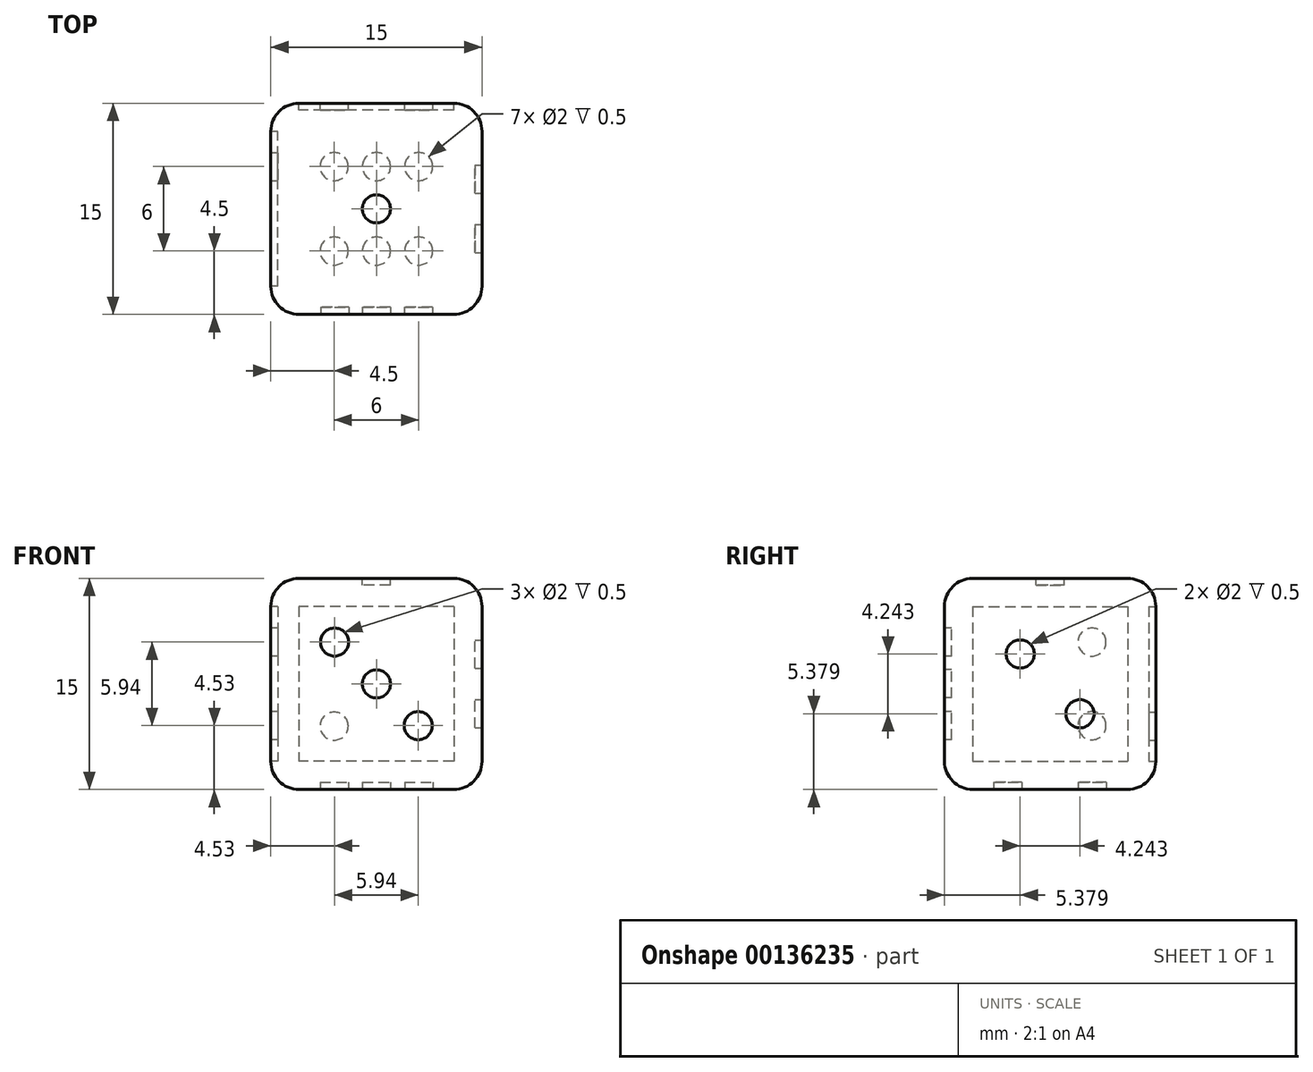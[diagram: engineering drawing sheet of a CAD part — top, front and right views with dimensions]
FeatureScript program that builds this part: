
annotation { "Feature Type Name" : "Feature", "Feature Type Description" : "" }
export const myFeature = defineFeature(function(context is Context, id is Id, definition is map)
    precondition{}
    {
        {
            var Q0;
            Q0=qCreatedBy(makeId("Top.planeOp"),FACE);
            var sketch = newSketch(context, id + "F0", { "sketchPlane" : qUnion([Q0])});
            skLineSegment(sketch, "E0.bottom", {"start": v(0, 0) * mm, "end": v(-15, 0) * mm});
            skLineSegment(sketch, "E0.top", {"start": v(0, 15) * mm, "end": v(-15, 15) * mm});
            skLineSegment(sketch, "E0.left", {"start": v(0, 0) * mm, "end": v(0, 15) * mm});
            skLineSegment(sketch, "E0.right", {"start": v(-15, 0) * mm, "end": v(-15, 15) * mm});
            skSolve(sketch);
        }
        {
            var Q0;
            Q0=makeQuery(id+"F0.imprint","IMPRINT",FACE,{"disambiguationData":[TD([[makeQuery(id+"F0.imprint","IMPRINT",EDGE,{"derivedFrom":sQuery(id+"F0.wireOp",EDGE,"E0.bottom")}),-1.0]])]});
            extrude(context, id + "F1", {"entities" : qUnion([Q0]), "depth" : 15 * mm});
        }
        {
            var Q0;
            Q0=makeQuery(id+"F1.opExtrude","SWEPT_EDGE",EDGE,{"disambiguationData":[OSD([sQuery(id+"F0.wireOp",EDGE,"E0.top"),sQuery(id+"F0.wireOp",EDGE,"E0.right")])]});
            var Q1;
            Q1=makeQuery(id+"F1.opExtrude","SWEPT_EDGE",EDGE,{"disambiguationData":[OSD([sQuery(id+"F0.wireOp",EDGE,"E0.top"),sQuery(id+"F0.wireOp",EDGE,"E0.left")])]});
            var Q2;
            Q2=makeQuery(id+"F1.opExtrude","SWEPT_EDGE",EDGE,{"disambiguationData":[OSD([sQuery(id+"F0.wireOp",EDGE,"E0.bottom"),sQuery(id+"F0.wireOp",EDGE,"E0.left")])]});
            var Q3;
            Q3=makeQuery(id+"F1.opExtrude","CAP_EDGE",EDGE,{"disambiguationData":[OSD([sQuery(id+"F0.wireOp",EDGE,"E0.bottom")])],"isStart":false});
            var Q4;
            Q4=makeQuery(id+"F1.opExtrude","CAP_EDGE",EDGE,{"disambiguationData":[OSD([sQuery(id+"F0.wireOp",EDGE,"E0.top")])],"isStart":true});
            var Q5;
            Q5=makeQuery(id+"F1.opExtrude","CAP_EDGE",EDGE,{"disambiguationData":[OSD([sQuery(id+"F0.wireOp",EDGE,"E0.top")])],"isStart":false});
            var Q6;
            Q6=makeQuery(id+"F1.opExtrude","SWEPT_EDGE",EDGE,{"disambiguationData":[OSD([sQuery(id+"F0.wireOp",EDGE,"E0.bottom"),sQuery(id+"F0.wireOp",EDGE,"E0.right")])]});
            var Q7;
            Q7=makeQuery(id+"F1.opExtrude","CAP_EDGE",EDGE,{"disambiguationData":[OSD([sQuery(id+"F0.wireOp",EDGE,"E0.bottom")])],"isStart":true});
            var Q8;
            Q8=makeQuery(id+"F1.opExtrude","CAP_EDGE",EDGE,{"disambiguationData":[OSD([sQuery(id+"F0.wireOp",EDGE,"E0.left")])],"isStart":true});
            var Q9;
            Q9=makeQuery(id+"F1.opExtrude","CAP_EDGE",EDGE,{"disambiguationData":[OSD([sQuery(id+"F0.wireOp",EDGE,"E0.left")])],"isStart":false});
            var Q10;
            Q10=makeQuery(id+"F1.opExtrude","CAP_EDGE",EDGE,{"disambiguationData":[OSD([sQuery(id+"F0.wireOp",EDGE,"E0.right")])],"isStart":true});
            var Q11;
            Q11=makeQuery(id+"F1.opExtrude","CAP_EDGE",EDGE,{"disambiguationData":[OSD([sQuery(id+"F0.wireOp",EDGE,"E0.right")])],"isStart":false});
            fillet(context, id + "F2", {"entities" : qUnion([Q0, Q1, Q2, Q3, Q4, Q5, Q6, Q7, Q8, Q9, Q10, Q11]), "radius" : 2 * mm, "tangentPropagation" : true, "allowEdgeOverflow" : false});
        }
        {
            var Q0;
            Q0=makeQuery(id+"F1.opExtrude","CAP_FACE",FACE,{"disambiguationData":[OSD([sQuery(id+"F0.wireOp",EDGE,"E0.bottom"),sQuery(id+"F0.wireOp",EDGE,"E0.top"),sQuery(id+"F0.wireOp",EDGE,"E0.left"),sQuery(id+"F0.wireOp",EDGE,"E0.right")])],"isStart":false});
            var sketch = newSketch(context, id + "F3", { "sketchPlane" : qUnion([Q0])});
            skCircle(sketch, "E1", {"center": v(-7.5, 7.5) * mm, "radius": 1 * mm});
            skPoint(sketch, "E1.centerSnap0", {"position": v(-13, 7.5) * mm});
            skSolve(sketch);
        }
        {
            var Q0;
            Q0=makeQuery(id+"F3.imprint","IMPRINT",FACE,{"disambiguationData":[TD([[makeQuery(id+"F3.imprint","IMPRINT",EDGE,{"derivedFrom":sQuery(id+"F3.wireOp",EDGE,"E1")}),1.0]])]});
            extrude(context, id + "F4", {"entities" : qUnion([Q0]), "operationType" : NewBodyOperationType.REMOVE, "oppositeDirection" : true, "depth" : 0.5 * mm});
        }
        {
            var Q0;
            Q0=makeQuery(id+"F1.opExtrude","CAP_FACE",FACE,{"disambiguationData":[OSD([sQuery(id+"F0.wireOp",EDGE,"E0.bottom"),sQuery(id+"F0.wireOp",EDGE,"E0.top"),sQuery(id+"F0.wireOp",EDGE,"E0.left"),sQuery(id+"F0.wireOp",EDGE,"E0.right")])],"isStart":true});
            var sketch = newSketch(context, id + "F5", { "sketchPlane" : qUnion([Q0])});
            skLineSegment(sketch, "E2", {"start": v(-13, -4.5) * mm, "end": v(-2, -4.5) * mm, "construction": true});
            skLineSegment(sketch, "E3", {"start": v(-13, -10.5) * mm, "end": v(-2, -10.5) * mm, "construction": true});
            skCircle(sketch, "E4", {"center": v(-10.5, -4.5) * mm, "radius": 1 * mm});
            skCircle(sketch, "E5", {"center": v(-7.5, -4.5) * mm, "radius": 1 * mm});
            skCircle(sketch, "E6", {"center": v(-4.5, -4.5) * mm, "radius": 1 * mm});
            skCircle(sketch, "E7", {"center": v(-10.5, -10.5) * mm, "radius": 1 * mm});
            skCircle(sketch, "E8", {"center": v(-7.5, -10.5) * mm, "radius": 1 * mm});
            skCircle(sketch, "E9", {"center": v(-4.5, -10.5) * mm, "radius": 1 * mm});
            skSolve(sketch);
        }
        {
            var Q0;
            Q0=makeQuery(id+"F5.imprint","IMPRINT",FACE,{"disambiguationData":[TD([[makeQuery(id+"F5.imprint","IMPRINT",EDGE,{"derivedFrom":sQuery(id+"F5.wireOp",EDGE,"E9")}),1.0]])]});
            var Q1;
            Q1=makeQuery(id+"F5.imprint","IMPRINT",FACE,{"disambiguationData":[TD([[makeQuery(id+"F5.imprint","IMPRINT",EDGE,{"derivedFrom":sQuery(id+"F5.wireOp",EDGE,"E8")}),1.0]])]});
            var Q2;
            Q2=makeQuery(id+"F5.imprint","IMPRINT",FACE,{"disambiguationData":[TD([[makeQuery(id+"F5.imprint","IMPRINT",EDGE,{"derivedFrom":sQuery(id+"F5.wireOp",EDGE,"E7")}),1.0]])]});
            var Q3;
            Q3=makeQuery(id+"F5.imprint","IMPRINT",FACE,{"disambiguationData":[TD([[makeQuery(id+"F5.imprint","IMPRINT",EDGE,{"derivedFrom":sQuery(id+"F5.wireOp",EDGE,"E4")}),1.0]])]});
            var Q4;
            Q4=makeQuery(id+"F5.imprint","IMPRINT",FACE,{"disambiguationData":[TD([[makeQuery(id+"F5.imprint","IMPRINT",EDGE,{"derivedFrom":sQuery(id+"F5.wireOp",EDGE,"E5")}),1.0]])]});
            var Q5;
            Q5=makeQuery(id+"F5.imprint","IMPRINT",FACE,{"disambiguationData":[TD([[makeQuery(id+"F5.imprint","IMPRINT",EDGE,{"derivedFrom":sQuery(id+"F5.wireOp",EDGE,"E6")}),1.0]])]});
            extrude(context, id + "F6", {"entities" : qUnion([Q0, Q1, Q2, Q3, Q4, Q5]), "operationType" : NewBodyOperationType.REMOVE, "oppositeDirection" : true, "depth" : 0.5 * mm});
        }
        {
            var Q0;
            Q0=makeQuery(id+"F1.opExtrude","SWEPT_FACE",FACE,{"disambiguationData":[OSD([sQuery(id+"F0.wireOp",EDGE,"E0.top")])]});
            var sketch = newSketch(context, id + "F7", { "sketchPlane" : qUnion([Q0])});
            skLineSegment(sketch, "E10", {"start": v(2, 10.5) * mm, "end": v(13, 10.5) * mm, "construction": true});
            skCircle(sketch, "E11", {"center": v(4.5, 10.5) * mm, "radius": 1 * mm});
            skCircle(sketch, "E12", {"center": v(10.5, 10.5) * mm, "radius": 1 * mm});
            skLineSegment(sketch, "E13", {"start": v(2, 7.5) * mm, "end": v(13, 7.5) * mm, "construction": true});
            skCircle(sketch, "E14.MirrorC", {"center": v(10.5, 4.5) * mm, "radius": 1 * mm});
            skCircle(sketch, "E15.MirrorC", {"center": v(4.5, 4.5) * mm, "radius": 1 * mm});
            skLineSegment(sketch, "E16.MirrorCS", {"start": v(2, 4.5) * mm, "end": v(13, 4.5) * mm, "construction": true});
            skSolve(sketch);
        }
        {
            var Q0;
            Q0=makeQuery(id+"F7.imprint","IMPRINT",FACE,{"disambiguationData":[TD([[makeQuery(id+"F7.imprint","IMPRINT",EDGE,{"derivedFrom":sQuery(id+"F7.wireOp",EDGE,"E12")}),1.0]])]});
            var Q1;
            Q1=makeQuery(id+"F7.imprint","IMPRINT",FACE,{"disambiguationData":[TD([[makeQuery(id+"F7.imprint","IMPRINT",EDGE,{"derivedFrom":sQuery(id+"F7.wireOp",EDGE,"E11")}),1.0]])]});
            var Q2;
            Q2=makeQuery(id+"F7.imprint","IMPRINT",FACE,{"disambiguationData":[TD([[makeQuery(id+"F7.imprint","IMPRINT",EDGE,{"derivedFrom":sQuery(id+"F7.wireOp",EDGE,"E15.MirrorC")}),-1.0]])]});
            var Q3;
            Q3=makeQuery(id+"F7.imprint","IMPRINT",FACE,{"disambiguationData":[TD([[makeQuery(id+"F7.imprint","IMPRINT",EDGE,{"derivedFrom":sQuery(id+"F7.wireOp",EDGE,"E14.MirrorC")}),-1.0]])]});
            extrude(context, id + "F8", {"entities" : qUnion([Q0, Q1, Q2, Q3]), "operationType" : NewBodyOperationType.REMOVE, "oppositeDirection" : true, "depth" : 0.5 * mm});
        }
        {
            var Q0;
            Q0=makeQuery(id+"F1.opExtrude","SWEPT_FACE",FACE,{"disambiguationData":[OSD([sQuery(id+"F0.wireOp",EDGE,"E0.bottom")])]});
            var sketch = newSketch(context, id + "F9", { "sketchPlane" : qUnion([Q0])});
            skLineSegment(sketch, "E17", {"start": v(-13, 13) * mm, "end": v(-2, 2) * mm, "construction": true});
            skCircle(sketch, "E18", {"center": v(-7.5, 7.5) * mm, "radius": 1 * mm});
            skCircle(sketch, "E19", {"center": v(-10.47, 10.47) * mm, "radius": 1 * mm});
            skCircle(sketch, "E20", {"center": v(-4.53, 4.53) * mm, "radius": 1 * mm});
            skSolve(sketch);
        }
        {
            var Q0;
            Q0=makeQuery(id+"F9.imprint","IMPRINT",FACE,{"disambiguationData":[TD([[makeQuery(id+"F9.imprint","IMPRINT",EDGE,{"derivedFrom":sQuery(id+"F9.wireOp",EDGE,"E19")}),1.0]])]});
            var Q1;
            Q1=makeQuery(id+"F9.imprint","IMPRINT",FACE,{"disambiguationData":[TD([[makeQuery(id+"F9.imprint","IMPRINT",EDGE,{"derivedFrom":sQuery(id+"F9.wireOp",EDGE,"E18")}),1.0]])]});
            var Q2;
            Q2=makeQuery(id+"F9.imprint","IMPRINT",FACE,{"disambiguationData":[TD([[makeQuery(id+"F9.imprint","IMPRINT",EDGE,{"derivedFrom":sQuery(id+"F9.wireOp",EDGE,"E20")}),1.0]])]});
            extrude(context, id + "F10", {"entities" : qUnion([Q0, Q1, Q2]), "operationType" : NewBodyOperationType.REMOVE, "oppositeDirection" : true, "depth" : 0.5 * mm});
        }
        {
            var Q0;
            Q0=makeQuery(id+"F1.opExtrude","SWEPT_FACE",FACE,{"disambiguationData":[OSD([sQuery(id+"F0.wireOp",EDGE,"E0.left")])]});
            var sketch = newSketch(context, id + "F11", { "sketchPlane" : qUnion([Q0])});
            skLineSegment(sketch, "E21", {"start": v(2, 13) * mm, "end": v(13, 2) * mm, "construction": true});
            skCircle(sketch, "E22", {"center": v(5.38, 9.62) * mm, "radius": 1 * mm});
            skCircle(sketch, "E23", {"center": v(9.62, 5.38) * mm, "radius": 1 * mm});
            skPoint(sketch, "E24", {"position": v(7.5, 7.5) * mm});
            skSolve(sketch);
        }
        {
            var Q0;
            Q0=makeQuery(id+"F11.imprint","IMPRINT",FACE,{"disambiguationData":[TD([[makeQuery(id+"F11.imprint","IMPRINT",EDGE,{"derivedFrom":sQuery(id+"F11.wireOp",EDGE,"E22")}),1.0]])]});
            var Q1;
            Q1=makeQuery(id+"F11.imprint","IMPRINT",FACE,{"disambiguationData":[TD([[makeQuery(id+"F11.imprint","IMPRINT",EDGE,{"derivedFrom":sQuery(id+"F11.wireOp",EDGE,"E23")}),1.0]])]});
            extrude(context, id + "F12", {"entities" : qUnion([Q0, Q1]), "operationType" : NewBodyOperationType.REMOVE, "oppositeDirection" : true, "depth" : 0.5 * mm});
        }
        {
            var Q0;
            Q0=makeQuery(id+"F1.opExtrude","SWEPT_FACE",FACE,{"disambiguationData":[OSD([sQuery(id+"F0.wireOp",EDGE,"E0.right")])]});
            var sketch = newSketch(context, id + "F13", { "sketchPlane" : qUnion([Q0])});
            skLineSegment(sketch, "E25", {"start": v(-13, 13) * mm, "end": v(-2, 2) * mm, "construction": true});
            skLineSegment(sketch, "E26", {"start": v(-2, 13) * mm, "end": v(-13, 2) * mm, "construction": true});
            skCircle(sketch, "E27", {"center": v(-7.5, 7.5) * mm, "radius": 1 * mm});
            skCircle(sketch, "E28", {"center": v(-4.53, 10.47) * mm, "radius": 1 * mm});
            skCircle(sketch, "E29", {"center": v(-4.53, 4.53) * mm, "radius": 1 * mm});
            skCircle(sketch, "E30.MirrorC", {"center": v(-10.47, 10.47) * mm, "radius": 1 * mm});
            skCircle(sketch, "E31.MirrorC", {"center": v(-10.47, 4.53) * mm, "radius": 1 * mm});
            skSolve(sketch);
        }
        {
            var Q0;
            Q0=makeQuery(id+"F13.imprint","IMPRINT",FACE,{"disambiguationData":[TD([[makeQuery(id+"F13.imprint","IMPRINT",EDGE,{"derivedFrom":sQuery(id+"F13.wireOp",EDGE,"E30.MirrorC")}),-1.0]])]});
            var Q1;
            Q1=makeQuery(id+"F13.imprint","IMPRINT",FACE,{"disambiguationData":[TD([[makeQuery(id+"F13.imprint","IMPRINT",EDGE,{"derivedFrom":sQuery(id+"F13.wireOp",EDGE,"E28")}),1.0]])]});
            var Q2;
            Q2=makeQuery(id+"F13.imprint","IMPRINT",FACE,{"disambiguationData":[TD([[makeQuery(id+"F13.imprint","IMPRINT",EDGE,{"derivedFrom":sQuery(id+"F13.wireOp",EDGE,"E27")}),1.0]])]});
            var Q3;
            Q3=makeQuery(id+"F13.imprint","IMPRINT",FACE,{"disambiguationData":[TD([[makeQuery(id+"F13.imprint","IMPRINT",EDGE,{"derivedFrom":sQuery(id+"F13.wireOp",EDGE,"E31.MirrorC")}),-1.0]])]});
            var Q4;
            Q4=makeQuery(id+"F13.imprint","IMPRINT",FACE,{"disambiguationData":[TD([[makeQuery(id+"F13.imprint","IMPRINT",EDGE,{"derivedFrom":sQuery(id+"F13.wireOp",EDGE,"E29")}),1.0]])]});
            extrude(context, id + "F14", {"entities" : qUnion([Q0, Q1, Q2, Q3, Q4]), "operationType" : NewBodyOperationType.REMOVE, "oppositeDirection" : true, "depth" : 0.5 * mm});
        }
    });
